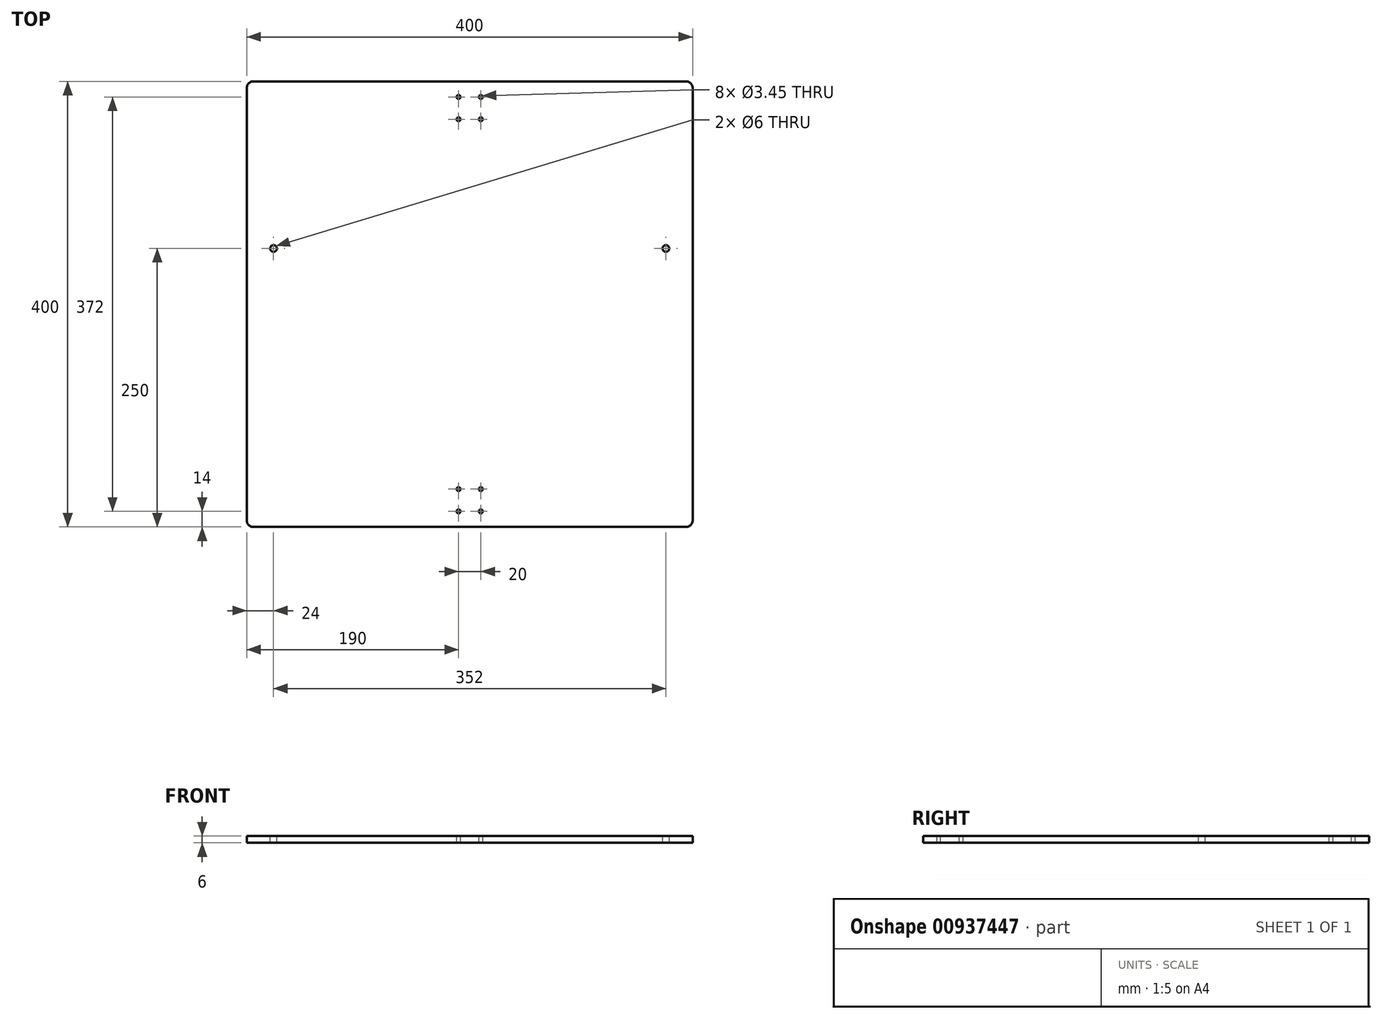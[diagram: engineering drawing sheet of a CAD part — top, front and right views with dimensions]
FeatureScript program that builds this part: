
annotation { "Feature Type Name" : "Feature", "Feature Type Description" : "" }
export const myFeature = defineFeature(function(context is Context, id is Id, definition is map)
    precondition{}
    {
        {
            var Q0;
            Q0=qCreatedBy(makeId("Top.planeOp"),FACE);
            var sketch = newSketch(context, id + "F0", { "sketchPlane" : qUnion([Q0])});
            skLineSegment(sketch, "E0.bottom", {"start": v(0, 0) * mm, "end": v(400, 0) * mm});
            skLineSegment(sketch, "E0.top", {"start": v(0, 400) * mm, "end": v(400, 400) * mm});
            skLineSegment(sketch, "E0.left", {"start": v(0, 0) * mm, "end": v(0, 400) * mm});
            skLineSegment(sketch, "E0.right", {"start": v(400, 0) * mm, "end": v(400, 400) * mm});
            skSolve(sketch);
        }
        {
            var Q0;
            Q0 = qSketchRegion(id + "F0", true);
            extrude(context, id + "F1", {"entities" : qUnion([Q0]), "depth" : 6 * mm, "offsetDistance" : 25 * mm});
        }
        {
            var Q0;
            Q0=makeQuery(id+"F1.opExtrude","SWEPT_EDGE",EDGE,{"disambiguationData":[OSD([sQuery(id+"F0.wireOp",EDGE,"E0.top"),sQuery(id+"F0.wireOp",EDGE,"E0.left")])]});
            var Q1;
            Q1=makeQuery(id+"F1.opExtrude","SWEPT_EDGE",EDGE,{"disambiguationData":[OSD([sQuery(id+"F0.wireOp",EDGE,"E0.top"),sQuery(id+"F0.wireOp",EDGE,"E0.right")])]});
            var Q2;
            Q2=makeQuery(id+"F1.opExtrude","SWEPT_EDGE",EDGE,{"disambiguationData":[OSD([sQuery(id+"F0.wireOp",EDGE,"E0.bottom"),sQuery(id+"F0.wireOp",EDGE,"E0.right")])]});
            var Q3;
            Q3=makeQuery(id+"F1.opExtrude","SWEPT_EDGE",EDGE,{"disambiguationData":[OSD([sQuery(id+"F0.wireOp",EDGE,"E0.bottom"),sQuery(id+"F0.wireOp",EDGE,"E0.left")])]});
            fillet(context, id + "F2", {"entities" : qUnion([Q0, Q1, Q2, Q3]), "radius" : 6 * mm, "tangentPropagation" : true, "allowEdgeOverflow" : false});
        }
        {
            var Q0;
            Q0=makeQuery(id+"F1.opExtrude","CAP_FACE",FACE,{"disambiguationData":[OSD([sQuery(id+"F0.wireOp",EDGE,"E0.bottom"),sQuery(id+"F0.wireOp",EDGE,"E0.top"),sQuery(id+"F0.wireOp",EDGE,"E0.left"),sQuery(id+"F0.wireOp",EDGE,"E0.right")])],"isStart":false});
            var sketch = newSketch(context, id + "F3", { "sketchPlane" : qUnion([Q0])});
            skLineSegment(sketch, "E1", {"start": v(24, 250) * mm, "end": v(376, 250) * mm, "construction": true});
            skLineSegment(sketch, "E2", {"start": v(200, 376) * mm, "end": v(200, 24) * mm, "construction": true});
            skPoint(sketch, "E2.startSnap0", {"position": v(200, 400) * mm});
            skLineSegment(sketch, "E3", {"start": v(200, 250) * mm, "end": v(200, 400) * mm, "construction": true});
            skCircle(sketch, "E4", {"center": v(24, 250) * mm, "radius": 3 * mm});
            skCircle(sketch, "E5", {"center": v(376, 250) * mm, "radius": 3 * mm});
            skLineSegment(sketch, "E6", {"start": v(0, 200) * mm, "end": v(200, 200) * mm, "construction": true});
            skLineSegment(sketch, "E7.bottom", {"start": v(190, 386) * mm, "end": v(210, 386) * mm, "construction": true});
            skLineSegment(sketch, "E7.top", {"start": v(190, 366) * mm, "end": v(210, 366) * mm, "construction": true});
            skLineSegment(sketch, "E7.left", {"start": v(190, 386) * mm, "end": v(190, 366) * mm, "construction": true});
            skLineSegment(sketch, "E7.right", {"start": v(210, 386) * mm, "end": v(210, 366) * mm, "construction": true});
            skLineSegment(sketch, "E8", {"start": v(200, 376) * mm, "end": v(190, 376) * mm});
            skLineSegment(sketch, "E9", {"start": v(190, 376) * mm, "end": v(200, 376) * mm, "construction": true});
            skLineSegment(sketch, "E10", {"start": v(200, 376) * mm, "end": v(200, 386) * mm, "construction": true});
            skCircle(sketch, "E11", {"center": v(190, 386) * mm, "radius": 1.73 * mm});
            skCircle(sketch, "E12", {"center": v(210, 386) * mm, "radius": 1.73 * mm});
            skCircle(sketch, "E13", {"center": v(210, 366) * mm, "radius": 1.73 * mm});
            skCircle(sketch, "E14", {"center": v(190, 366) * mm, "radius": 1.73 * mm});
            skLineSegment(sketch, "E15.bottom", {"start": v(190, 34) * mm, "end": v(210, 34) * mm, "construction": true});
            skLineSegment(sketch, "E15.top", {"start": v(190, 14) * mm, "end": v(210, 14) * mm, "construction": true});
            skLineSegment(sketch, "E15.left", {"start": v(190, 34) * mm, "end": v(190, 14) * mm, "construction": true});
            skLineSegment(sketch, "E15.right", {"start": v(210, 34) * mm, "end": v(210, 14) * mm, "construction": true});
            skLineSegment(sketch, "E16", {"start": v(200, 24) * mm, "end": v(200, 34) * mm, "construction": true});
            skLineSegment(sketch, "E17", {"start": v(200, 24) * mm, "end": v(190, 24) * mm, "construction": true});
            skCircle(sketch, "E18", {"center": v(190, 34) * mm, "radius": 1.73 * mm});
            skCircle(sketch, "E19", {"center": v(210, 34) * mm, "radius": 1.73 * mm});
            skCircle(sketch, "E20", {"center": v(210, 14) * mm, "radius": 1.73 * mm});
            skCircle(sketch, "E21", {"center": v(190, 14) * mm, "radius": 1.73 * mm});
            skSolve(sketch);
        }
        {
            var Q0;
            Q0 = qSketchRegion(id + "F3", true);
            extrude(context, id + "F4", {"entities" : qUnion([Q0]), "operationType" : NewBodyOperationType.REMOVE, "endBound" : BoundingType.UP_TO_NEXT, "oppositeDirection" : true, "depth" : 25 * mm, "offsetDistance" : 25 * mm});
        }
    });
